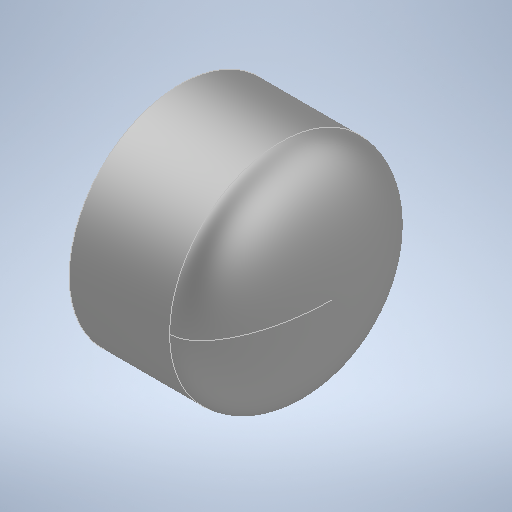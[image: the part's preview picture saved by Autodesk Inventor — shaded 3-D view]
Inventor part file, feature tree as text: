
AUTODESK INVENTOR PART (.ipt)
format: ipt  version: 2025 (Build 290162010, 162A)  size: 364,544 bytes
history: native  units: in
note: dims shown in document units (in); Inventor stores cm internally (conversion verified against a paired STEP export)
features: revolve x1, other x1
ambient origin geometry x8: Origin, YZ Plane, XZ Plane, XY Plane, X Axis, Y Axis, Z Axis, Center Point
bodies: Solid1 (feature_tree)
feature tree (2):
  revolve  "Revolve1"  [1 undecoded]
  other  "Axis1"
note: 1 required parameter value undecoded (feature->parameter linkage not recoverable at this tier; creation-order binding heuristic only, values carry confidence <= 0.55)
